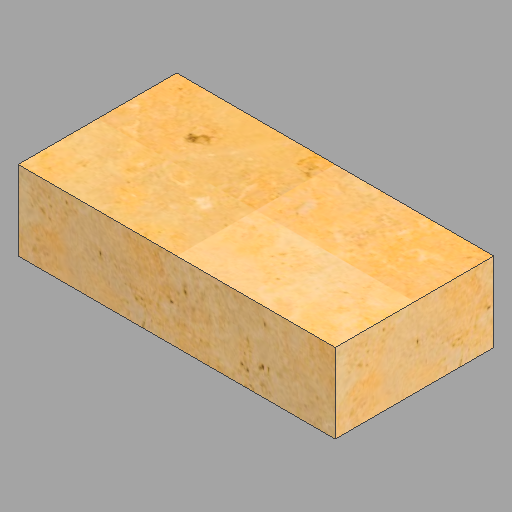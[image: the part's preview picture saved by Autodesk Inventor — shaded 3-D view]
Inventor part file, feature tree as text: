
AUTODESK INVENTOR PART (.ipt)
format: ipt  version: 2023 (Build 270158030, 158C)  size: 309,760 bytes
history: native  units: in
note: dims shown in document units (in); Inventor stores cm internally (conversion verified against a paired STEP export)
features: other x1, extrude x1, sketch x1
ambient origin geometry x8: Origin, YZ Plane, XZ Plane, XY Plane, X Axis, Y Axis, Z Axis, Center Point
bodies: Solid1 (feature_tree)
feature tree (3):
  other  "4x8x2 - 39"
  extrude  "Extrusion1"  Depth=4.0in
  sketch  "Sketch1"  dims[d0=8.0in d1=4.0in d2=2.0in d3=0.0in]
